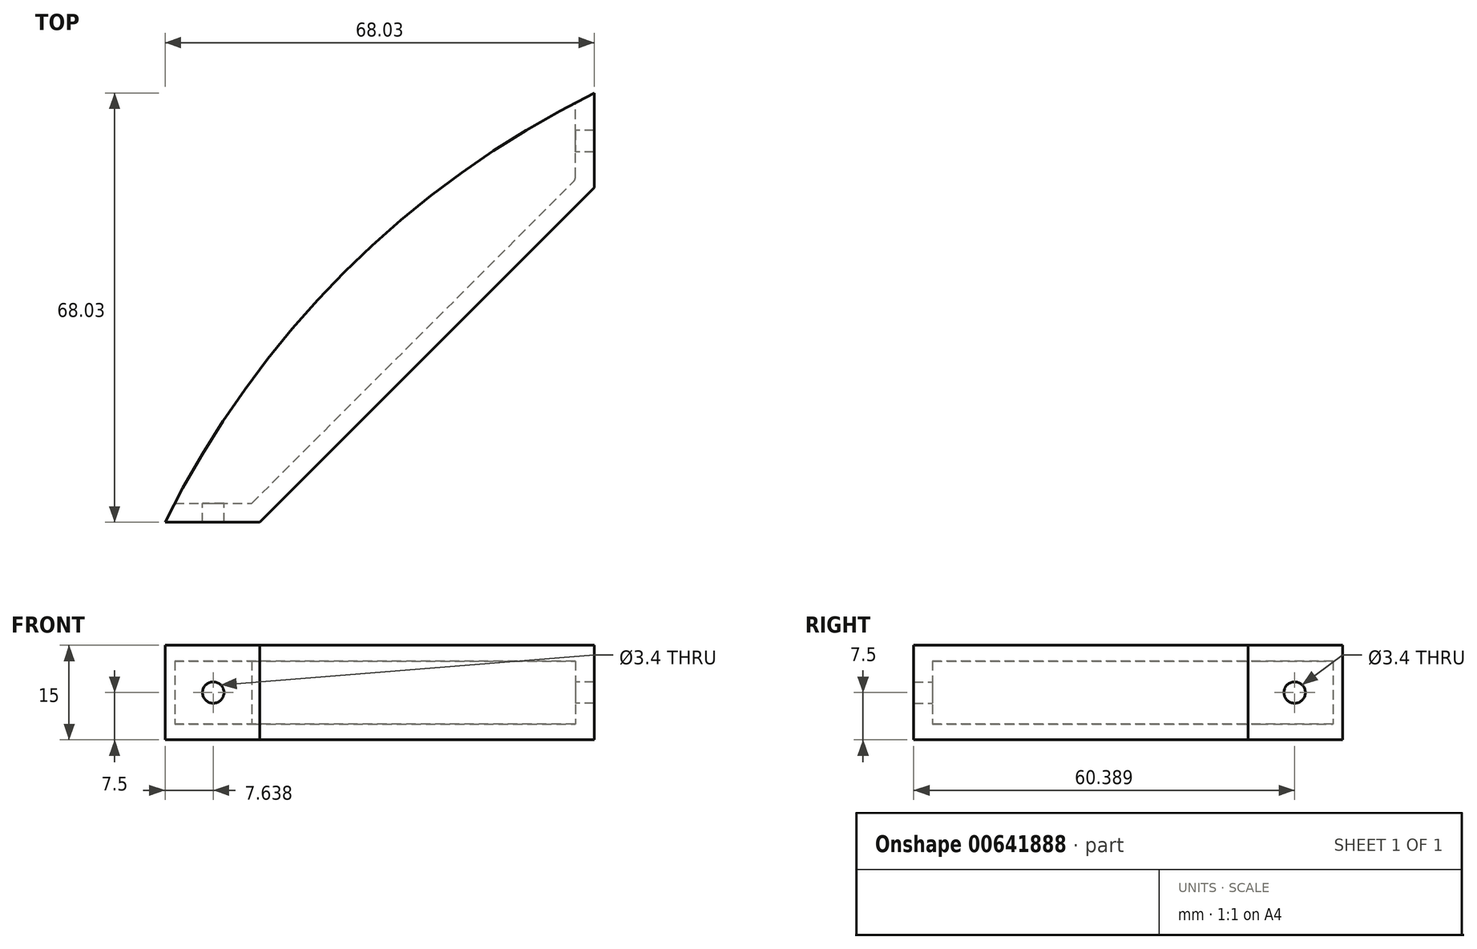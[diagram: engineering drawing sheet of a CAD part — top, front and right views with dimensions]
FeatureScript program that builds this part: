
annotation { "Feature Type Name" : "Feature", "Feature Type Description" : "" }
export const myFeature = defineFeature(function(context is Context, id is Id, definition is map)
    precondition{}
    {
        {
            var Q0;
            Q0=qCreatedBy(makeId("Top.planeOp"),FACE);
            var sketch = newSketch(context, id + "F0", { "sketchPlane" : qUnion([Q0])});
            skLineSegment(sketch, "E0", {"start": v(0, 0) * mm, "end": v(-53.03, -53.03) * mm});
            skLineSegment(sketch, "E1", {"start": v(-53.03, -53.03) * mm, "end": v(-68.03, -53.03) * mm});
            skLineSegment(sketch, "E2", {"start": v(0, 0) * mm, "end": v(0, 15) * mm});
            skArc(sketch, "E3", {"start": v(0, 15) * mm, "mid": v(-39.62, -13.41) * mm, "end": v(-68.03, -53.03) * mm});
            skSolve(sketch);
        }
        {
            var Q0;
            Q0=makeQuery(id+"F0.imprint","IMPRINT",FACE,{"disambiguationData":[TD([[makeQuery(id+"F0.imprint","IMPRINT",EDGE,{"derivedFrom":sQuery(id+"F0.wireOp",EDGE,"E0")}),-1.0]])]});
            extrude(context, id + "F1", {"entities" : qUnion([Q0]), "depth" : 2.5 * mm, "offsetDistance" : 25 * mm});
        }
        {
            var Q0;
            Q0=makeQuery(id+"F1.opExtrude","CAP_FACE",FACE,{"disambiguationData":[OSD([sQuery(id+"F0.wireOp",EDGE,"E0"),sQuery(id+"F0.wireOp",EDGE,"E1"),sQuery(id+"F0.wireOp",EDGE,"E2"),sQuery(id+"F0.wireOp",EDGE,"E3")])],"isStart":false});
            var sketch = newSketch(context, id + "F2", { "sketchPlane" : qUnion([Q0])});
            skLineSegment(sketch, "E4", {"start": v(0, 15) * mm, "end": v(0, 0) * mm});
            skLineSegment(sketch, "E5", {"start": v(0, 0) * mm, "end": v(-53.03, -53.03) * mm});
            skLineSegment(sketch, "E6", {"start": v(-53.03, -53.03) * mm, "end": v(-68.03, -53.03) * mm});
            skLineSegment(sketch, "E7", {"start": v(-66.5, -50.03) * mm, "end": v(-54.28, -50.03) * mm});
            skLineSegment(sketch, "E8", {"start": v(-54.28, -50.03) * mm, "end": v(-3, 1.24) * mm});
            skLineSegment(sketch, "E9", {"start": v(-3, 1.24) * mm, "end": v(-3, 13.48) * mm});
            skArc(sketch, "E10", {"start": v(0, 15) * mm, "mid": v(-1.5, 14.25) * mm, "end": v(-3, 13.48) * mm});
            skArc(sketch, "E11.trimOffspring", {"start": v(-66.5, -50.03) * mm, "mid": v(-67.28, -51.53) * mm, "end": v(-68.03, -53.03) * mm});
            skSolve(sketch);
        }
        {
            var Q0;
            Q0=makeQuery(id+"F2.imprint","IMPRINT",FACE,{"disambiguationData":[TD([[makeQuery(id+"F2.imprint","IMPRINT",EDGE,{"derivedFrom":sQuery(id+"F2.wireOp",EDGE,"E4")}),1.0]])]});
            extrude(context, id + "F3", {"entities" : qUnion([Q0]), "operationType" : NewBodyOperationType.ADD, "depth" : 10 * mm, "offsetDistance" : 25 * mm});
        }
        {
            var Q0;
            Q0=makeQuery(id+"F3.opExtrude","CAP_FACE",FACE,{"disambiguationData":[OSD([sQuery(id+"F2.wireOp",EDGE,"E4"),sQuery(id+"F2.wireOp",EDGE,"E5"),sQuery(id+"F2.wireOp",EDGE,"E6"),sQuery(id+"F2.wireOp",EDGE,"E7"),sQuery(id+"F2.wireOp",EDGE,"E8"),sQuery(id+"F2.wireOp",EDGE,"E9"),sQuery(id+"F2.wireOp",EDGE,"E10"),sQuery(id+"F2.wireOp",EDGE,"E11.trimOffspring")])],"isStart":false});
            var sketch = newSketch(context, id + "F4", { "sketchPlane" : qUnion([Q0])});
            skLineSegment(sketch, "E12", {"start": v(-68.03, -53.03) * mm, "end": v(-53.03, -53.03) * mm});
            skLineSegment(sketch, "E13", {"start": v(-53.03, -53.03) * mm, "end": v(0, 0) * mm});
            skLineSegment(sketch, "E14", {"start": v(0, 0) * mm, "end": v(0, 15) * mm});
            skArc(sketch, "E15", {"start": v(0, 15) * mm, "mid": v(-39.62, -13.41) * mm, "end": v(-68.03, -53.03) * mm});
            skSolve(sketch);
        }
        {
            var Q0;
            Q0 = qSketchRegion(id + "F4", true);
            extrude(context, id + "F5", {"entities" : qUnion([Q0]), "operationType" : NewBodyOperationType.ADD, "depth" : 2.5 * mm, "offsetDistance" : 25 * mm});
        }
        {
            var Q0;
            Q0=makeQuery(id+"F3.opExtrude","SWEPT_FACE",FACE,{"disambiguationData":[OSD([sQuery(id+"F2.wireOp",EDGE,"E9")])]});
            var sketch = newSketch(context, id + "F6", { "sketchPlane" : qUnion([Q0])});
            skCircle(sketch, "E16", {"center": v(-7.36, 7.5) * mm, "radius": 1.7 * mm});
            skPoint(sketch, "E16.centerSnap0", {"position": v(-13.48, 7.5) * mm});
            skPoint(sketch, "E16.centerSnap1", {"position": v(-7.36, 12.5) * mm});
            skSolve(sketch);
        }
        {
            var Q0;
            Q0=makeQuery(id+"F6.imprint","IMPRINT",FACE,{"disambiguationData":[TD([[makeQuery(id+"F6.imprint","IMPRINT",EDGE,{"derivedFrom":sQuery(id+"F6.wireOp",EDGE,"E16")}),1.0]])]});
            extrude(context, id + "F7", {"entities" : qUnion([Q0]), "operationType" : NewBodyOperationType.REMOVE, "oppositeDirection" : true, "depth" : 25 * mm, "offsetDistance" : 25 * mm});
        }
        {
            var Q0;
            Q0=makeQuery(id+"F3.opExtrude","SWEPT_FACE",FACE,{"disambiguationData":[OSD([sQuery(id+"F2.wireOp",EDGE,"E7")])]});
            var sketch = newSketch(context, id + "F8", { "sketchPlane" : qUnion([Q0])});
            skCircle(sketch, "E17", {"center": v(60.4, 7.5) * mm, "radius": 1.7 * mm});
            skPoint(sketch, "E17.centerSnap0", {"position": v(60.4, 12.5) * mm});
            skPoint(sketch, "E17.centerSnap1", {"position": v(66.5, 7.5) * mm});
            skSolve(sketch);
        }
        {
            var Q0;
            Q0=makeQuery(id+"F8.imprint","IMPRINT",FACE,{"disambiguationData":[TD([[makeQuery(id+"F8.imprint","IMPRINT",EDGE,{"derivedFrom":sQuery(id+"F8.wireOp",EDGE,"E17")}),1.0]])]});
            extrude(context, id + "F9", {"entities" : qUnion([Q0]), "operationType" : NewBodyOperationType.REMOVE, "oppositeDirection" : true, "depth" : 25 * mm, "offsetDistance" : 25 * mm});
        }
        {
            var Q0;
            Q0=makeQuery(id+"F3.opExtrude","CAP_EDGE",EDGE,{"disambiguationData":[OSD([sQuery(id+"F2.wireOp",EDGE,"E8")])],"isStart":false});
            var Q1;
            Q1=makeQuery(id+"F3.opExtrude","SWEPT_EDGE",EDGE,{"disambiguationData":[OSD([sQuery(id+"F2.wireOp",EDGE,"E8"),sQuery(id+"F2.wireOp",EDGE,"E9")])]});
            var Q2;
            Q2=makeQuery(id+"F3.opExtrude","CAP_EDGE",EDGE,{"disambiguationData":[OSD([sQuery(id+"F2.wireOp",EDGE,"E9")])],"isStart":false});
            var Q3;
            Q3=makeQuery(id+"F3.opExtrude","CAP_EDGE",EDGE,{"disambiguationData":[OSD([sQuery(id+"F2.wireOp",EDGE,"E7")])],"isStart":false});
            var Q4;
            Q4=makeQuery(id+"F3.opExtrude","CAP_EDGE",EDGE,{"disambiguationData":[OSD([sQuery(id+"F2.wireOp",EDGE,"E9")])],"isStart":true});
            var Q5;
            Q5=makeQuery(id+"F3.opExtrude","CAP_EDGE",EDGE,{"disambiguationData":[OSD([sQuery(id+"F2.wireOp",EDGE,"E8")])],"isStart":true});
            var Q6;
            Q6=makeQuery(id+"F3.opExtrude","CAP_EDGE",EDGE,{"disambiguationData":[OSD([sQuery(id+"F2.wireOp",EDGE,"E7")])],"isStart":true});
            fillet(context, id + "F10", {"entities" : qUnion([Q0, Q1, Q2, Q3, Q4, Q5, Q6]), "radius" : 1 * mm, "tangentPropagation" : true, "allowEdgeOverflow" : false});
        }
    });
